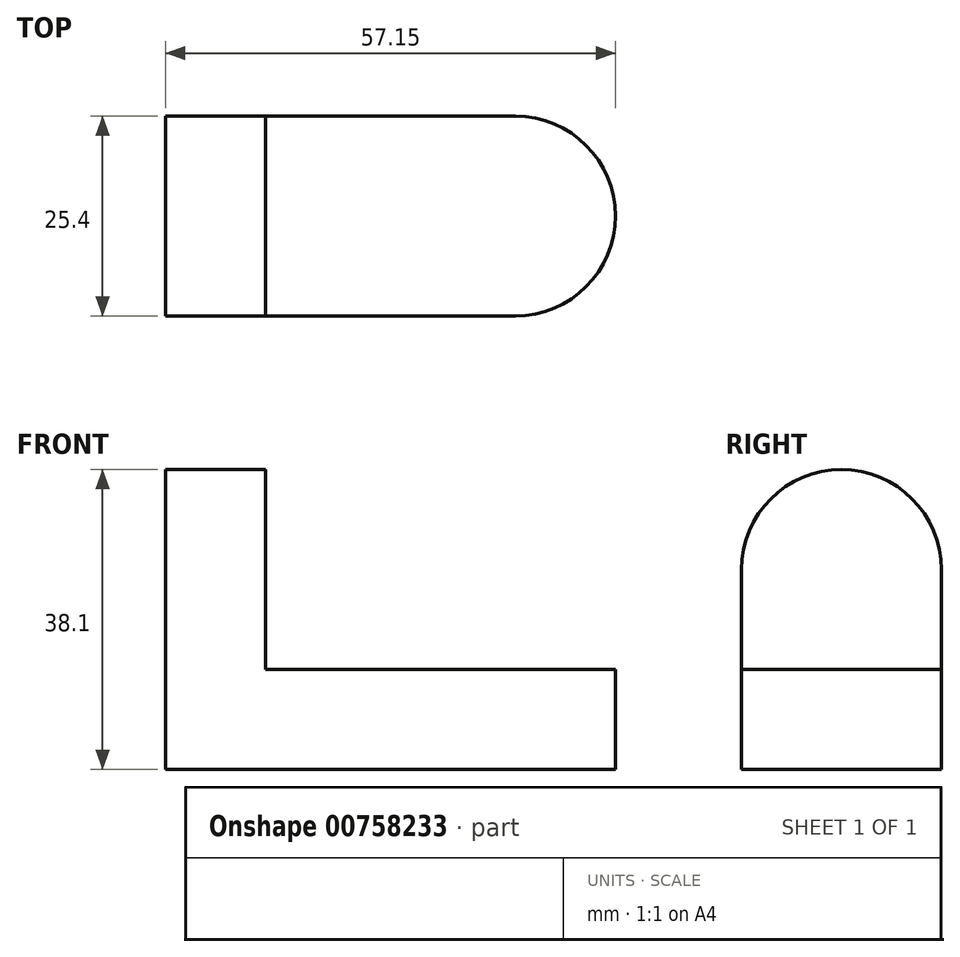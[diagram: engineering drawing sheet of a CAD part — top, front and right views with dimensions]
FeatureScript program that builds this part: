
annotation { "Feature Type Name" : "Feature", "Feature Type Description" : "" }
export const myFeature = defineFeature(function(context is Context, id is Id, definition is map)
    precondition{}
    {
        {
            var Q0;
            Q0=qCreatedBy(makeId("Front.planeOp"),FACE);
            var sketch = newSketch(context, id + "F0", { "sketchPlane" : qUnion([Q0])});
            skLineSegment(sketch, "E0", {"start": v(0, 0) * mm, "end": v(0, 25.4) * mm});
            skLineSegment(sketch, "E1", {"start": v(0, 25.4) * mm, "end": v(12.7, 25.4) * mm});
            skLineSegment(sketch, "E2", {"start": v(12.7, 25.4) * mm, "end": v(12.7, 12.7) * mm});
            skLineSegment(sketch, "E3", {"start": v(12.7, 12.7) * mm, "end": v(44.45, 12.7) * mm});
            skLineSegment(sketch, "E4", {"start": v(44.45, 12.7) * mm, "end": v(44.45, 0) * mm});
            skLineSegment(sketch, "E5", {"start": v(44.45, 0) * mm, "end": v(0, 0) * mm});
            skSolve(sketch);
        }
        {
            var Q0;
            Q0=makeQuery(id+"F0.imprint","IMPRINT",FACE,{"disambiguationData":[TD([[makeQuery(id+"F0.imprint","IMPRINT",EDGE,{"derivedFrom":sQuery(id+"F0.wireOp",EDGE,"E0")}),-1.0]])]});
            extrude(context, id + "F1", {"entities" : qUnion([Q0]), "depth" : 25.4 * mm, "offsetDistance" : 25.4 * mm});
        }
        {
            var Q0;
            Q0=makeQuery(id+"F1.opExtrude","SWEPT_FACE",FACE,{"disambiguationData":[OSD([sQuery(id+"F0.wireOp",EDGE,"E3")])]});
            var sketch = newSketch(context, id + "F2", { "sketchPlane" : qUnion([Q0])});
            skArc(sketch, "E6", {"start": v(44.45, -25.4) * mm, "mid": v(57.15, -12.7) * mm, "end": v(44.45, 0) * mm});
            skSolve(sketch);
        }
        {
            var Q0;
            Q0=makeQuery(id+"F2.imprint","IMPRINT",FACE,{"disambiguationData":[TD([[makeQuery(id+"F2.imprint","IMPRINT",EDGE,{"derivedFrom":sQuery(id+"F2.wireOp",EDGE,"E6")}),1.0]])]});
            extrude(context, id + "F3", {"entities" : qUnion([Q0]), "operationType" : NewBodyOperationType.ADD, "depth" : 0 * mm, "offsetDistance" : 25.4 * mm, "hasSecondDirection" : true, "secondDirectionOppositeDirection" : true, "secondDirectionDepth" : 12.7 * mm});
        }
        {
            var Q0;
            Q0=makeQuery(id+"F1.opExtrude","SWEPT_FACE",FACE,{"disambiguationData":[OSD([sQuery(id+"F0.wireOp",EDGE,"E2")])]});
            var sketch = newSketch(context, id + "F4", { "sketchPlane" : qUnion([Q0])});
            skArc(sketch, "E7", {"start": v(0, 25.4) * mm, "mid": v(-12.7, 38.1) * mm, "end": v(-25.4, 25.4) * mm});
            skSolve(sketch);
        }
        {
            var Q0;
            Q0=makeQuery(id+"F4.imprint","IMPRINT",FACE,{"disambiguationData":[TD([[makeQuery(id+"F4.imprint","IMPRINT",EDGE,{"derivedFrom":sQuery(id+"F4.wireOp",EDGE,"E7")}),1.0]])]});
            extrude(context, id + "F5", {"entities" : qUnion([Q0]), "operationType" : NewBodyOperationType.ADD, "depth" : 0 * mm, "offsetDistance" : 25.4 * mm, "hasSecondDirection" : true, "secondDirectionOppositeDirection" : true, "secondDirectionDepth" : 12.7 * mm});
        }
    });
